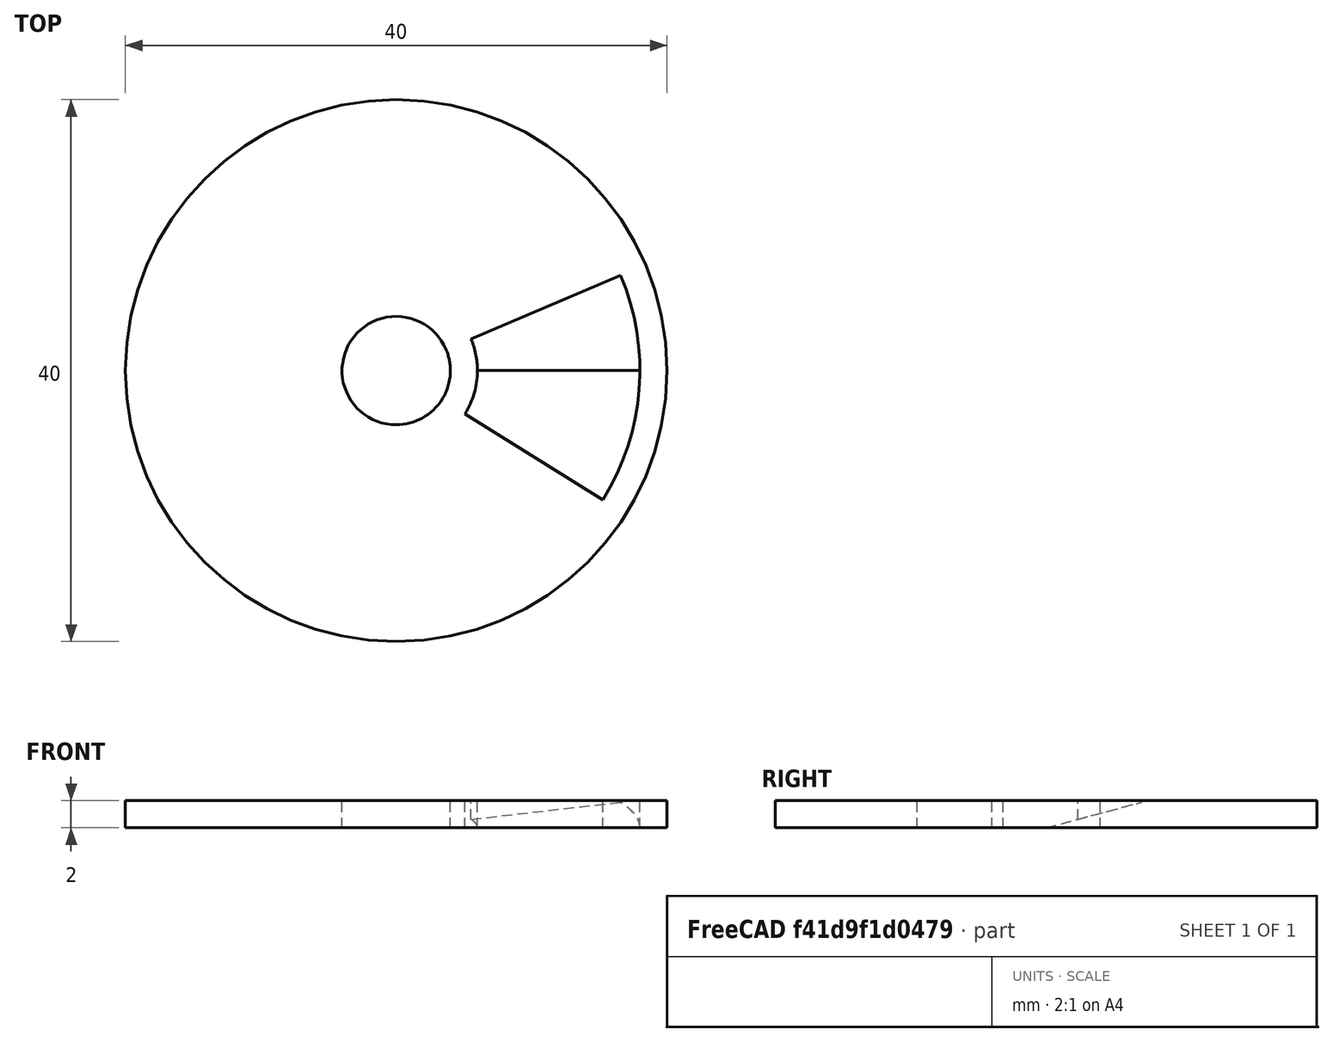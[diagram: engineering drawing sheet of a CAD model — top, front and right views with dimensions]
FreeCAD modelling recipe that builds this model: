
FCSTD DOCUMENT  (FreeCAD 0.14R3700 (Git))
Label: trampilla salida v1.3 version para imprimir
License: CC-BY 3.0
LicenseURL: http://creativecommons.org/licenses/by/3.0/
objects: Part::Cylinder×8, Part::Cut×8, Part::MultiCommon×3, Part::Box×2, Part::MultiFuse×1
note: 22 computed .brp shape members not serialized (recipe doc carries the construction recipe); baked Part::Feature solids carry a one-line shape summary decoded from their .brp

FEATURE [Part::Cylinder] Cylinder
  Angle = 360
  Height = 2
  Radius = 20
FEATURE [Part::Cylinder] Cylinder002
  Angle = 360
  Height = 10
  Radius = 6
FEATURE [Part::Cylinder] Cylinder003
  Angle = 360
  Height = 10
  Radius = 4
FEATURE [Part::Cylinder] Cylinder004
  Angle = 360
  Height = 10
  Placement = pos=(0,0,21) rot=(0,0,1;0rad)
  Radius = 18
FEATURE [Part::Box] Box007  label="Cube"
  Height = 31
  Length = 30
  Placement = pos=(0,-20,0) rot=(0,0,1;0rad)
  Width = 40
FEATURE [Part::Cut] Cut
  Base = -> Cylinder004
  Placement = pos=(0,0,-25) rot=(0,0,-1;2.63545rad)
  Tool = -> Box007
FEATURE [Part::Box] Box008  label="Cube008"
  Height = 31
  Length = 30
  Placement = pos=(0,-20,0) rot=(0,0,1;0rad)
  Width = 40
FEATURE [Part::Cylinder] Cylinder005
  Angle = 360
  Height = 10
  Placement = pos=(0,0,21) rot=(0,0,1;0rad)
  Radius = 18
FEATURE [Part::Cut] Cut001
  Base = -> Cylinder005
  Placement = pos=(0,0,-25) rot=(0,0,-1;0.453786rad)
  Tool = -> Box008
FEATURE [Part::MultiCommon] Common
  Placement = pos=(0,0,0) rot=(0,0,-1;1.67552rad)
  Shapes = -> [Cut,Cut001]
FEATURE [Part::Cut] Cut002
  Base = -> Cylinder005
  Placement = pos=(0,0,-25) rot=(0,0,-1;0.453786rad)
  Tool = -> Box008
FEATURE [Part::Cut] Cut003
  Base = -> Cylinder004
  Placement = pos=(0,0,-25) rot=(0,0,1;3.64774rad)
  Tool = -> Box007
FEATURE [Part::MultiCommon] Common001
  Placement = pos=(0,0,14) rot=(0,0,1;0.087266rad)
  Shapes = -> [Cut003,Cut002]
FEATURE [Part::Cylinder] Cylinder006
  Angle = 360
  Height = 2
  Placement = pos=(-4,-1,9) rot=(0,1,0;0.261799rad)
  Radius = 20
FEATURE [Part::Cut] Cut004
  Base = -> Cylinder
  Tool = -> Common
FEATURE [Part::MultiCommon] Common002
  Placement = pos=(0,0,-10) rot=(0,0,-1;1.5708rad)
  Shapes = -> [Common001,Cylinder006]
FEATURE [Part::Cut] Cut005
  Base = -> Cylinder002
  Tool = -> Cylinder003
FEATURE [Part::Cylinder] Cylinder007
  Angle = 360
  Height = 10
  Placement = pos=(0,0,2) rot=(0,0,1;0rad)
  Radius = 26
FEATURE [Part::MultiFuse] Fusion
  Shapes = -> [Cut004,Common002,Cut005]
FEATURE [Part::Cut] Cut006
  Base = -> Fusion
  Tool = -> Cylinder007
FEATURE [Part::Cylinder] Cylinder008
  Angle = 360
  Height = 16
  Placement = pos=(0,0,-7) rot=(0,0,1;0rad)
  Radius = 4
FEATURE [Part::Cut] Cut007
  Base = -> Cut006
  Tool = -> Cylinder008
